# Revit family: 65162101
name_source: partatom
category: Plumbing Fixtures
units: mm (PartAtom-declared; Revit-internal decimal feet)

## family parameters
Always vertical = Yes
Cut with Voids When Loaded = No
OmniClass Number = 23.45.55.00
OmniClass Title = Sanitary Faucets, Wastes
Part Type = Normal
Room Calculation Point = No
Round Connector Dimension = Use Diameter
Shared = No
Work Plane-Based = No

## types (1)
- 65162101 Shower system
    2D/3D/BIM Files URL = http://static.hansa.com
    3D View = https://static.hansa.com
    Additional Features = Torrent water flow, protected against back-flow in domestic use (according to DIN EN 1717)
    Advanced Features = Flexible length / can be shortened
    AssetType = Fixed
    BIMObjectName = 65162101
    Backflow Prevention EN1717 = EB
    BodyMaterial = Brass
    Brand = HANSA
    CO2 Emissions (A1-A3) = 36.07
    CO2 Emissions (A4) = 0.95
    CO2 Emissions (B7) = 3126.6
    CO2 Emissions (C2) = 0.07
    CO2 Emissions (C3) = 0.07
    CO2 Emissions (C4) = 1.97
    CO2 Emissions (D) = -23.57
    Catalog Drawing URL = http://static.hansa.com
    Category = Bathroom;Shower
    CloseOffRating = 0
    Color = Chrome
    Connection = Eccentric coupling(s)
    Connection Size = G1/2
    Default Elevation = 0 mm  [stored 0 ft]
    Dimension Drawing URL = http://static.hansa.com
    Diverter = Turn operated diverter;Integrated into flow control handle
    DurationUnit = Year
    EAN Number = 4015474277229
    EN Standard = EN 1111, EN 1112, EN 1113
    ETIM Class Number = EC011329 Shower mixing tap
    FDV Document URL = http://www.hansa.com
    FaucetMainMaterial = Brass
    Features = Thermostatic
    Finish = Polished
    Flow Drawing URL = http://static.hansa.com
    Flow Rate At 300kPa = 0.3 L/s
    FlowCoefficient = 0
    Group = Shower system
    Hand Shower Size = Ø 94 mm
    IfcExportAs = IfcValveType
    IfcExportType = FAUCET
    Installation Type = Wall mounted
    Installation Width = cc150 ± 15 mm
    Installation and Maintenance Guide URL = http://static.hansa.com
    Interactive AR View URL = https://static.hansa.com
    Lever Handle = Temperature control handle;Flow control handle
    Manufacturer = HANSA
    ManufacturerName = HANSA
    ManufacturerURL = http://www.hansa.com
    Market = Austria;Belgium;Czech Republic;Germany;Spain;France;International;Italy;Netherlands;Slovakia
    Material = Brass
    Max. Hot Water Supply = 65 °C
    Mechanical Parts = Thermostatic cartridge for automatic temperature control;Fixing Set;Non-return valve(s);Litter filter(s)
    Mobile Product Information URL = http://mpi.hansa.com
    Model = 65162101 Shower system
    ModelReference = 65162101
    NBSDescription = Shower mixers
    NBSReference = 45-35-70/335
    Name = 65162101 Shower system
    Name_en = 65162101 Shower system
    NominalDepth = 583 mm
    NominalHeight = 1665 mm
    NominalWidth = 537 mm  [stored 1.76181 ft]
    Over Head Shower Size = 257 x 197 mm
    Product Code = 65162101
    Product Family = HANSAFIT
    Product Image URL = http://static.hansa.com
    Product URL = http://static.hansa.com
    ProductInformation = Thermostatic rain shower faucet with a spout and a hand shower
    RainShowerNominalDepth = 583 mm
    RainShowerNominalHeight = 1665 mm
    RainShowerNominalWidth = 285 mm
    Sales Package dimensions (LxWxH) = 1024 x 225 x 114
    Shape = Sculptured
    Shower Parts = Hand shower;Shower rail;Overhead shower;Adjustable shower rail bracket;Soap dish;Shower holder;Shower hose (2000 mm);Eco flow control;Rotatable ball joint connection;Anti limescale technology (easy to clean)
    Shower Spray = Normal;Refreshing;Relaxing
    Shower Spray Number = 3 shower sprays
    Size = Rain shower: 285x583x1665 mm / Tray: 200x145x125 mm
    SoapTrayNominalDepth = 149 mm
    SoapTrayNominalHeight = 128 mm
    SoapTrayNominalWidth = 199 mm
    Spare-Part Information URL = http://static.hansa.com
    Spout Projection = 485 mm
    Spout Type = Fixed spout
    Surface treatment = Chrome
    Technical DataSheet URL = http://www.hansa.com
    Temperature Adjustments = The housing of the fittings conducts minimal heat;Safety stop against scalding at 38°C
    UNSPSC Class Number = 30181805 Combination fixed and hand held shower head
    URL Declaration of Conformity = http://static.hansa.com
    URL Environmental Product Declaration EPD = http://www.hansa.com system.pdf
    URL REACH = http://static.hansa.com
    Uniclass2 = Pr_40_30_96_81
    Uniclass2015Description = Shower thermostatic water supply sets
    Uniclass2015Reference = Pr_40_20_87_81
    Version = 1
    VersionDate = 11/07/2023
    Warranty Information URL = http://warranty.hansa.com
    WarrantyDescription = http://warranty.hansa.com
    WarrantyDurationUnit = Year
    Working Pressure = 100 - 1000 kPa
    WorkingPressure = 100 - 1000 kPa

note: [stored X ft] marks values corroborated as IEEE doubles in the binary element streams (Revit-internal decimal feet)

## geometry (parser evidence)
native form markers: Sweep x7
no freeform markers — native parametric forms only
